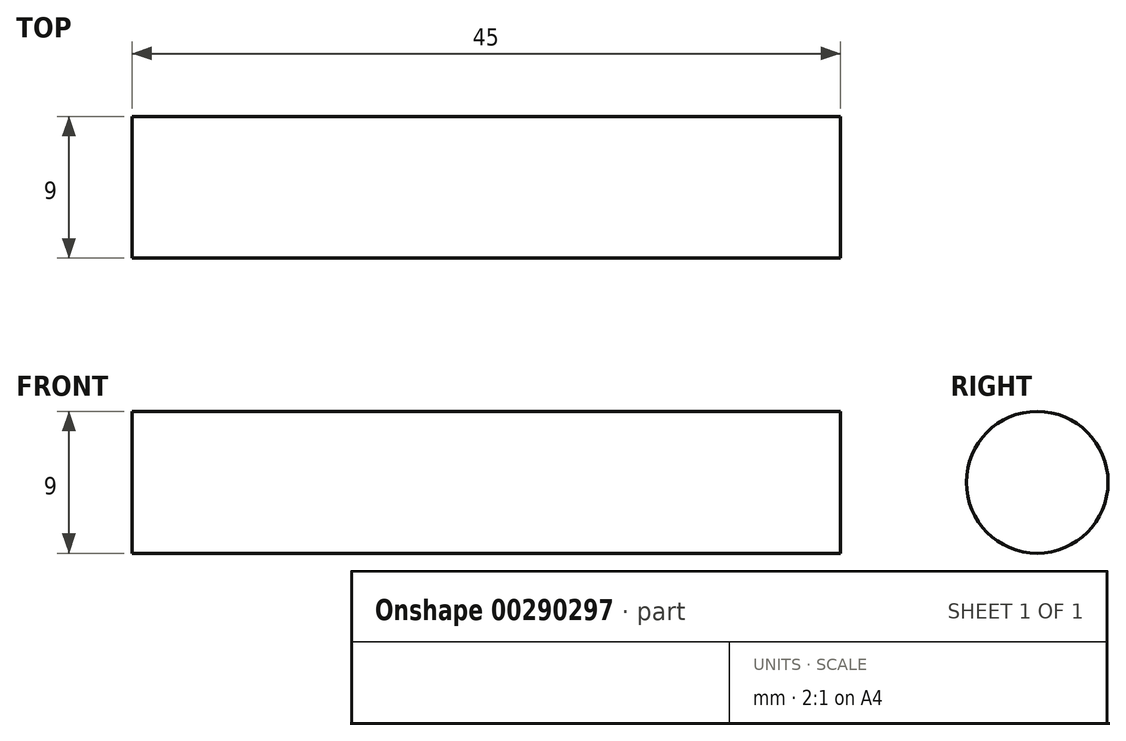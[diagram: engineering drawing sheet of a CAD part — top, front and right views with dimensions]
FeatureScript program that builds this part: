
annotation { "Feature Type Name" : "Feature", "Feature Type Description" : "" }
export const myFeature = defineFeature(function(context is Context, id is Id, definition is map)
    precondition{}
    {
        {
            var Q0;
            Q0=qCreatedBy(makeId("Front.planeOp"),FACE);
            var sketch = newSketch(context, id + "F0", { "sketchPlane" : qUnion([Q0])});
            skLineSegment(sketch, "E0", {"start": v(-11.74, 0) * mm, "end": v(-11.74, 4.5) * mm});
            skLineSegment(sketch, "E1", {"start": v(-11.74, 4.5) * mm, "end": v(33.26, 4.5) * mm});
            skLineSegment(sketch, "E2", {"start": v(33.26, 4.5) * mm, "end": v(33.26, 0) * mm});
            skLineSegment(sketch, "E3", {"start": v(-11.74, 0) * mm, "end": v(33.26, 0) * mm});
            skSolve(sketch);
        }
        {
            var Q0;
            Q0 = qSketchRegion(id + "F0", true);
            var Q1;
            Q1=sQuery(id+"F0.wireOp",EDGE,"E3");
            revolve(context, id + "F1", {"entities" : qUnion([Q0]), "axis" : qUnion([Q1]), "revolveType" : RevolveType.FULL});
        }
    });
